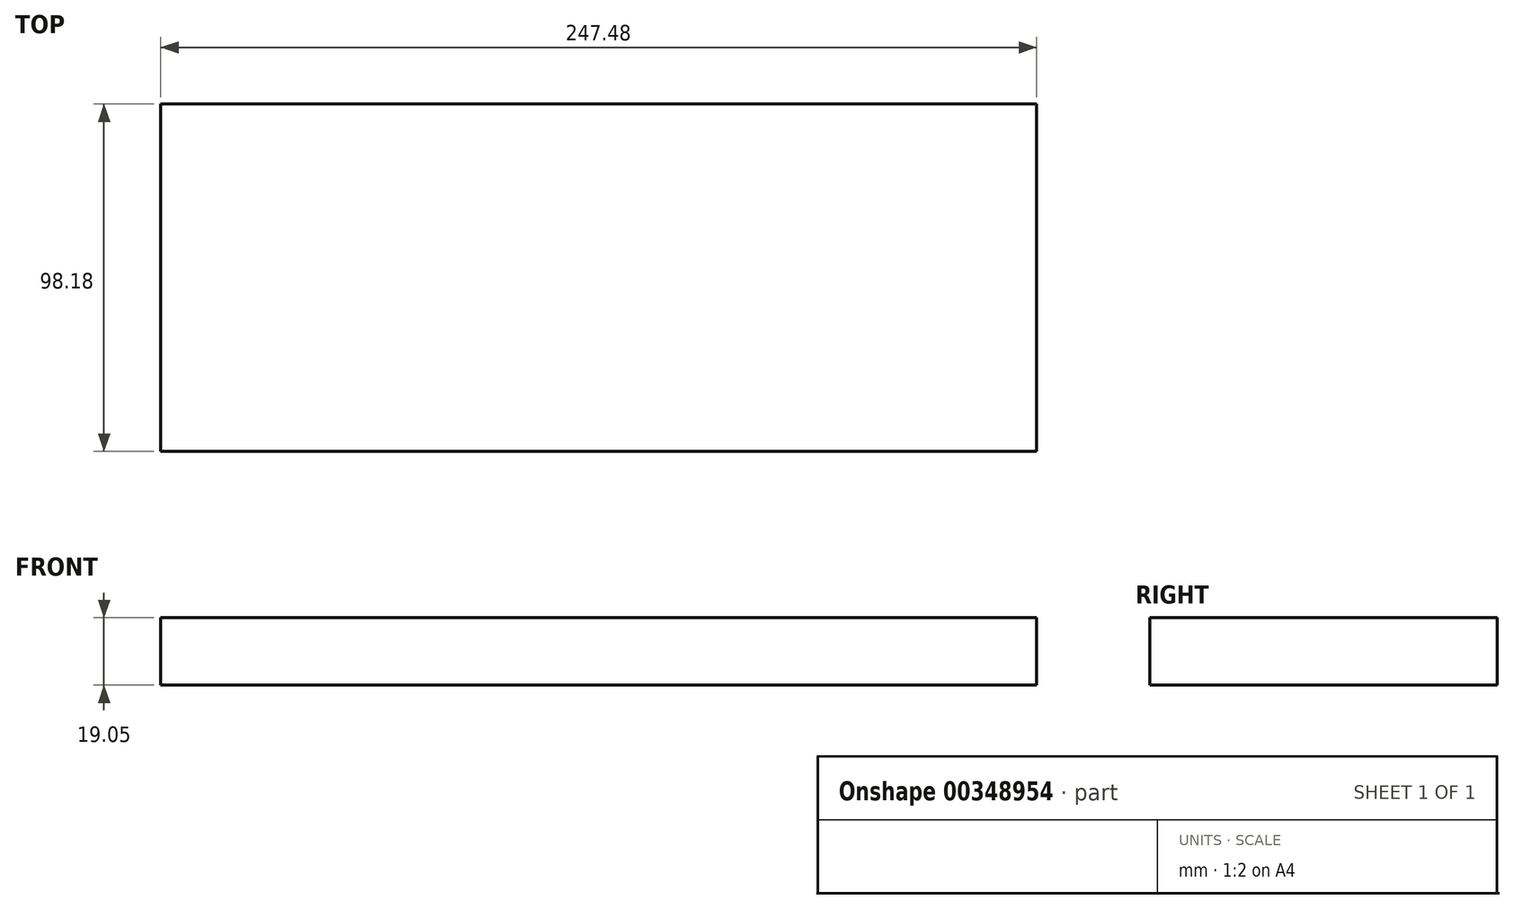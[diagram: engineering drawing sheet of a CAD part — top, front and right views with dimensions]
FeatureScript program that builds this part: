
annotation { "Feature Type Name" : "Feature", "Feature Type Description" : "" }
export const myFeature = defineFeature(function(context is Context, id is Id, definition is map)
    precondition{}
    {
        {
            var Q0;
            Q0=qCreatedBy(makeId("Top.planeOp"),FACE);
            var sketch = newSketch(context, id + "F0", { "sketchPlane" : qUnion([Q0])});
            skLineSegment(sketch, "E0.bottom", {"start": v(-141.97, -45.71) * mm, "end": v(105.5, -45.71) * mm});
            skLineSegment(sketch, "E0.top", {"start": v(-141.97, 52.47) * mm, "end": v(105.5, 52.47) * mm});
            skLineSegment(sketch, "E0.left", {"start": v(-141.97, -45.71) * mm, "end": v(-141.97, 52.47) * mm});
            skLineSegment(sketch, "E0.right", {"start": v(105.5, -45.71) * mm, "end": v(105.5, 52.47) * mm});
            skLineSegment(sketch, "E1.bottom", {"start": v(0, -61.85) * mm, "end": v(-33.66, -61.85) * mm});
            skLineSegment(sketch, "E1.top", {"start": v(0, -76.9) * mm, "end": v(-33.66, -76.9) * mm});
            skLineSegment(sketch, "E1.left", {"start": v(0, -61.85) * mm, "end": v(0, -76.9) * mm});
            skLineSegment(sketch, "E1.right", {"start": v(-33.66, -61.85) * mm, "end": v(-33.66, -76.9) * mm});
            skSolve(sketch);
        }
        {
            var Q0;
            Q0=makeQuery(id+"F0.imprint","IMPRINT",FACE,{"disambiguationData":[TD([[makeQuery(id+"F0.imprint","IMPRINT",EDGE,{"derivedFrom":sQuery(id+"F0.wireOp",EDGE,"E0.bottom")}),1.0]])]});
            extrude(context, id + "F1", {"entities" : qUnion([Q0]), "depth" : 19.05 * mm});
        }
    });
